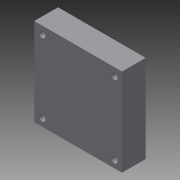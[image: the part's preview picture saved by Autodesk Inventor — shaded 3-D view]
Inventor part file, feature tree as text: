
AUTODESK INVENTOR PART (.ipt)
format: ipt  version: 2013 (Build 170138000, 138)  size: 83,456 bytes
history: native  units: mm
features: extrude x1, sketch x1
ambient origin geometry x8: Origin, YZ Plane, XZ Plane, XY Plane, X Axis, Y Axis, Z Axis, Center Point
bodies: Solid1 (feature_tree)
feature tree (2):
  extrude  "Extrusion1"  Depth=39.9mm
  sketch  "Sketch1"  dims[d0=39.9mm d2=39.9mm d3=3.0mm d4=3.0mm d5=3.0mm d6=3.0mm d7=3.5mm d8=3.5mm d9=3.5mm d10=3.5mm d11=3.5mm d12=3.5mm d13=3.5mm d14=10.8mm d15=0.0mm]
